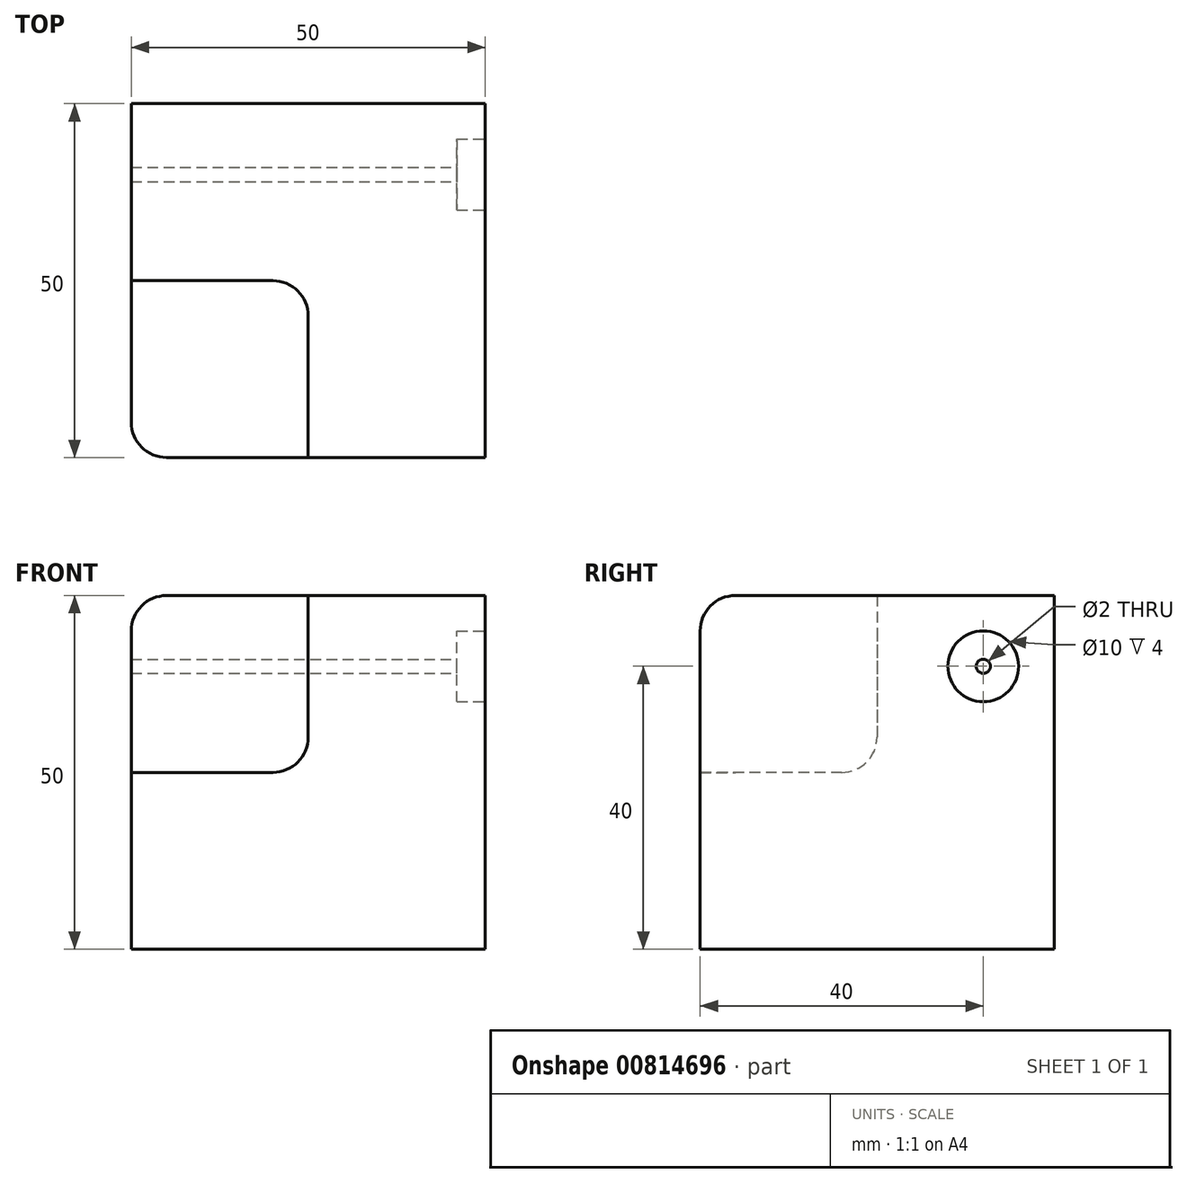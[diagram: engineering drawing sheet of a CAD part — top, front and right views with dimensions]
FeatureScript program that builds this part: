
annotation { "Feature Type Name" : "Feature", "Feature Type Description" : "" }
export const myFeature = defineFeature(function(context is Context, id is Id, definition is map)
    precondition{}
    {
        {
            var Q0;
            Q0=qCreatedBy(makeId("Top.planeOp"),FACE);
            var sketch = newSketch(context, id + "F0", { "sketchPlane" : qUnion([Q0])});
            skLineSegment(sketch, "E0.bottom", {"start": v(25, 25) * mm, "end": v(-25, 25) * mm});
            skLineSegment(sketch, "E0.top", {"start": v(25, -25) * mm, "end": v(-25, -25) * mm});
            skLineSegment(sketch, "E0.left", {"start": v(25, 25) * mm, "end": v(25, -25) * mm});
            skLineSegment(sketch, "E0.right", {"start": v(-25, 25) * mm, "end": v(-25, -25) * mm});
            skPoint(sketch, "E0.middle", {"position": v(0, 0) * mm});
            skSolve(sketch);
        }
        {
            var Q0;
            Q0=makeQuery(id+"F0.imprint","IMPRINT",FACE,{"disambiguationData":[TD([[makeQuery(id+"F0.imprint","IMPRINT",EDGE,{"derivedFrom":sQuery(id+"F0.wireOp",EDGE,"E0.bottom")}),1.0]])]});
            extrude(context, id + "F1", {"entities" : qUnion([Q0]), "depth" : 50 * mm, "offsetDistance" : 25 * mm});
        }
        {
            var Q0;
            Q0=makeQuery(id+"F1.opExtrude","SWEPT_FACE",FACE,{"disambiguationData":[OSD([sQuery(id+"F0.wireOp",EDGE,"E0.left")])]});
            var sketch = newSketch(context, id + "F2", { "sketchPlane" : qUnion([Q0])});
            skPoint(sketch, "E1", {"position": v(15, 40) * mm});
            skSolve(sketch);
        }
        {
            var Q0;
            Q0=sQuery(id+"F2.wireOp",VERTEX,"E1");
            var Q1;
            Q1=makeQuery(id+"F1.opExtrude","SWEPT_BODY",BODY,{"disambiguationData":[OSD([sQuery(id+"F0.wireOp",EDGE,"E0.bottom"),sQuery(id+"F0.wireOp",EDGE,"E0.top"),sQuery(id+"F0.wireOp",EDGE,"E0.left"),sQuery(id+"F0.wireOp",EDGE,"E0.right")])]});
            hole(context, id + "F3", {"style" : HoleStyle.C_BORE, "endStyle" : HoleEndStyle.THROUGH, "holeDiameter" : 2 * mm, "cBoreDiameter" : 10 * mm, "cBoreDepth" : 4 * mm, "majorDiameter" : 5 * mm, "isTappedThrough" : true, "tappedDepth" : 12 * mm, "tapClearance" : 3, "locations" : qUnion([Q0]), "scope" : qUnion([Q1])});
        }
        {
            var Q0;
            Q0=makeQuery(id+"F1.opExtrude","SWEPT_FACE",FACE,{"disambiguationData":[OSD([sQuery(id+"F0.wireOp",EDGE,"E0.top")])]});
            var sketch = newSketch(context, id + "F4", { "sketchPlane" : qUnion([Q0])});
            skLineSegment(sketch, "E2.bottom", {"start": v(-25, 50) * mm, "end": v(0, 50) * mm});
            skLineSegment(sketch, "E2.top", {"start": v(-25, 25) * mm, "end": v(0, 25) * mm});
            skLineSegment(sketch, "E2.left", {"start": v(-25, 50) * mm, "end": v(-25, 25) * mm});
            skLineSegment(sketch, "E2.right", {"start": v(0, 50) * mm, "end": v(0, 25) * mm});
            skSolve(sketch);
        }
        {
            var Q0;
            Q0=makeQuery(id+"F4.imprint","IMPRINT",FACE,{"disambiguationData":[TD([[makeQuery(id+"F4.imprint","IMPRINT",EDGE,{"derivedFrom":sQuery(id+"F4.wireOp",EDGE,"E2.bottom")}),1.0]])]});
            extrude(context, id + "F5", {"entities" : qUnion([Q0]), "operationType" : NewBodyOperationType.REMOVE, "oppositeDirection" : true, "depth" : 25 * mm, "offsetDistance" : 25 * mm});
        }
        {
            var Q0;
            Q0=makeQuery(id+"F5.boolean.opBoolean","COPY",EDGE,{"derivedFrom":makeQuery(id+"F5.opExtrude","CAP_EDGE",EDGE,{"disambiguationData":[OSD([sQuery(id+"F4.wireOp",EDGE,"E2.top")])],"isStart":false})});
            var Q1;
            Q1=makeQuery(id+"F5.boolean.opBoolean","COPY",EDGE,{"derivedFrom":makeQuery(id+"F5.opExtrude","CAP_EDGE",EDGE,{"disambiguationData":[OSD([sQuery(id+"F4.wireOp",EDGE,"E2.left")])],"isStart":false})});
            var Q2;
            Q2=makeQuery(id+"F5.boolean.opBoolean","COPY",EDGE,{"derivedFrom":makeQuery(id+"F5.opExtrude","CAP_EDGE",EDGE,{"disambiguationData":[OSD([sQuery(id+"F4.wireOp",EDGE,"E2.right")])],"isStart":false})});
            var Q3;
            Q3=makeQuery(id+"F5.boolean.opBoolean","COPY",EDGE,{"derivedFrom":makeQuery(id+"F5.opExtrude","SWEPT_EDGE",EDGE,{"disambiguationData":[OSD([sQuery(id+"F0.wireOp",EDGE,"E0.top"),sQuery(id+"F4.wireOp",EDGE,"E2.bottom"),sQuery(id+"F4.wireOp",EDGE,"E2.right")])]})});
            var Q4;
            Q4=makeQuery(id+"F5.boolean.opBoolean","COPY",EDGE,{"derivedFrom":makeQuery(id+"F5.opExtrude","CAP_EDGE",EDGE,{"disambiguationData":[OSD([sQuery(id+"F4.wireOp",EDGE,"E2.right")])],"isStart":true})});
            var Q5;
            Q5=makeQuery(id+"F5.boolean.opBoolean","COPY",EDGE,{"derivedFrom":makeQuery(id+"F5.opExtrude","CAP_EDGE",EDGE,{"disambiguationData":[OSD([sQuery(id+"F4.wireOp",EDGE,"E2.top")])],"isStart":true})});
            var Q6;
            Q6=makeQuery(id+"F5.boolean.opBoolean","COPY",EDGE,{"derivedFrom":makeQuery(id+"F5.opExtrude","SWEPT_EDGE",EDGE,{"disambiguationData":[OSD([sQuery(id+"F4.wireOp",EDGE,"E2.top"),sQuery(id+"F4.wireOp",EDGE,"E2.right")])]})});
            var Q7;
            Q7=makeQuery(id+"F1.opExtrude","CAP_EDGE",EDGE,{"disambiguationData":[OSD([sQuery(id+"F0.wireOp",EDGE,"E0.right")])],"isStart":false});
            var Q8;
            Q8=makeQuery(id+"F1.opExtrude","CAP_EDGE",EDGE,{"disambiguationData":[OSD([sQuery(id+"F0.wireOp",EDGE,"E0.top")])],"isStart":false});
            var Q9;
            Q9=makeQuery(id+"F1.opExtrude","SWEPT_EDGE",EDGE,{"disambiguationData":[OSD([sQuery(id+"F0.wireOp",EDGE,"E0.top"),sQuery(id+"F0.wireOp",EDGE,"E0.right")])]});
            fillet(context, id + "F6", {"entities" : qUnion([Q0, Q1, Q2, Q3, Q4, Q5, Q6, Q7, Q8, Q9]), "radius" : 5 * mm, "tangentPropagation" : true, "allowEdgeOverflow" : false});
        }
    });
